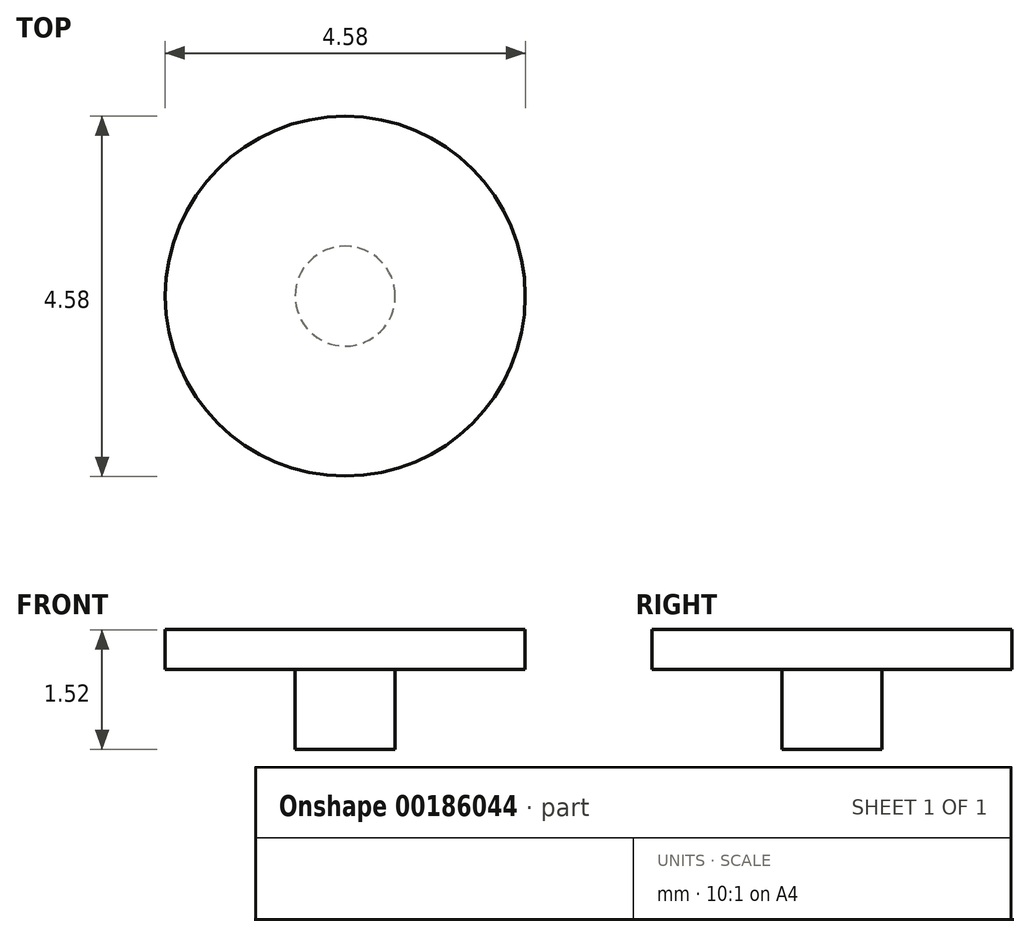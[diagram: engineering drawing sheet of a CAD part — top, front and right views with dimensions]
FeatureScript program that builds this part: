
annotation { "Feature Type Name" : "Feature", "Feature Type Description" : "" }
export const myFeature = defineFeature(function(context is Context, id is Id, definition is map)
    precondition{}
    {
        {
            var Q0;
            Q0=qCreatedBy(makeId("Top.planeOp"),FACE);
            var sketch = newSketch(context, id + "F0", { "sketchPlane" : qUnion([Q0])});
            skCircle(sketch, "E0", {"center": v(0, 0) * mm, "radius": 0.64 * mm});
            skSolve(sketch);
        }
        {
            var Q0;
            Q0 = qSketchRegion(id + "F0", true);
            extrude(context, id + "F1", {"entities" : qUnion([Q0]), "depth" : 1.02 * mm});
        }
        {
            var Q0;
            Q0=makeQuery(id+"F1.opExtrude","CAP_FACE",FACE,{"disambiguationData":[OSD([sQuery(id+"F0.wireOp",EDGE,"E0")])],"isStart":false});
            var sketch = newSketch(context, id + "F2", { "sketchPlane" : qUnion([Q0])});
            skCircle(sketch, "E1", {"center": v(0, 0) * mm, "radius": 2.29 * mm});
            skSolve(sketch);
        }
        {
            var Q0;
            Q0=makeQuery(id+"F2.imprint","IMPRINT",FACE,{"disambiguationData":[TD([[makeQuery(id+"F2.imprint","IMPRINT",EDGE,{"derivedFrom":makeQuery(id+"F1.opExtrude","CAP_EDGE",EDGE,{"disambiguationData":[OSD([sQuery(id+"F0.wireOp",EDGE,"E0")])],"isStart":false})}),1.0]])]});
            var Q1;
            Q1=makeQuery(id+"F2.imprint","IMPRINT",FACE,{"disambiguationData":[TD([[makeQuery(id+"F2.imprint","IMPRINT",EDGE,{"derivedFrom":sQuery(id+"F2.wireOp",EDGE,"E1")}),1.0]])]});
            extrude(context, id + "F3", {"entities" : qUnion([Q0, Q1]), "operationType" : NewBodyOperationType.ADD, "depth" : 0.5 * mm});
        }
    });
